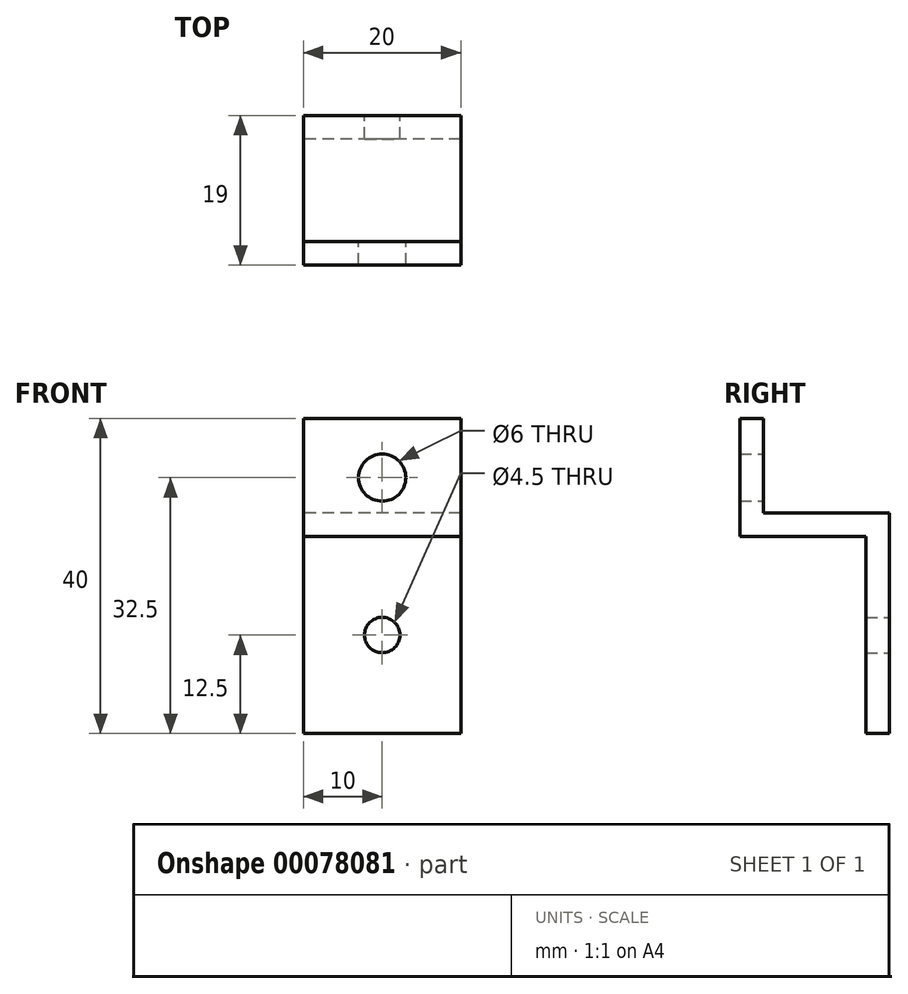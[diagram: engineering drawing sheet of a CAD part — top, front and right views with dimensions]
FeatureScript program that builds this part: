
annotation { "Feature Type Name" : "Feature", "Feature Type Description" : "" }
export const myFeature = defineFeature(function(context is Context, id is Id, definition is map)
    precondition{}
    {
        {
            var Q0;
            Q0=qCreatedBy(makeId("Right.planeOp"),FACE);
            var sketch = newSketch(context, id + "F0", { "sketchPlane" : qUnion([Q0])});
            skLineSegment(sketch, "E0", {"start": v(0, 0) * mm, "end": v(0, 15) * mm});
            skLineSegment(sketch, "E1", {"start": v(0, 15) * mm, "end": v(3, 15) * mm});
            skLineSegment(sketch, "E2", {"start": v(3, 15) * mm, "end": v(3, 3) * mm});
            skLineSegment(sketch, "E3", {"start": v(3, 3) * mm, "end": v(19, 3) * mm});
            skLineSegment(sketch, "E4", {"start": v(19, 3) * mm, "end": v(19, -25) * mm});
            skLineSegment(sketch, "E5", {"start": v(19, -25) * mm, "end": v(16, -25) * mm});
            skLineSegment(sketch, "E6", {"start": v(16, -25) * mm, "end": v(16, 0) * mm});
            skLineSegment(sketch, "E7", {"start": v(16, 0) * mm, "end": v(0, 0) * mm});
            skSolve(sketch);
        }
        {
            var Q0;
            Q0 = qSketchRegion(id + "F0", true);
            extrude(context, id + "F1", {"entities" : qUnion([Q0]), "depth" : 20 * mm, "offsetDistance" : 25 * mm});
        }
        {
            var Q0;
            Q0=makeQuery(id+"F1.opExtrude","SWEPT_FACE",FACE,{"disambiguationData":[OSD([sQuery(id+"F0.wireOp",EDGE,"E0")])]});
            var sketch = newSketch(context, id + "F2", { "sketchPlane" : qUnion([Q0])});
            skPoint(sketch, "E8", {"position": v(10, 7.5) * mm});
            skSolve(sketch);
        }
        {
            var Q0;
            Q0=makeQuery(id+"F1.opExtrude","SWEPT_FACE",FACE,{"disambiguationData":[OSD([sQuery(id+"F0.wireOp",EDGE,"E6")])]});
            var sketch = newSketch(context, id + "F3", { "sketchPlane" : qUnion([Q0])});
            skPoint(sketch, "E9", {"position": v(10, -12.5) * mm});
            skSolve(sketch);
        }
        {
            var Q0;
            Q0=sQuery(id+"F2.wireOp",VERTEX,"E8");
            var Q1;
            Q1=makeQuery(id+"F1.opExtrude","SWEPT_BODY",BODY,{"disambiguationData":[OSD([sQuery(id+"F0.wireOp",EDGE,"E0"),sQuery(id+"F0.wireOp",EDGE,"E1"),sQuery(id+"F0.wireOp",EDGE,"E2"),sQuery(id+"F0.wireOp",EDGE,"E3"),sQuery(id+"F0.wireOp",EDGE,"E4"),sQuery(id+"F0.wireOp",EDGE,"E5"),sQuery(id+"F0.wireOp",EDGE,"E6"),sQuery(id+"F0.wireOp",EDGE,"E7")])]});
            hole(context, id + "F4", {"style" : HoleStyle.SIMPLE, "endStyle" : HoleEndStyle.THROUGH, "holeDiameter" : 6 * mm, "majorDiameter" : 5 * mm, "tappedDepth" : 12 * mm, "tapClearance" : 3, "locations" : qUnion([Q0]), "scope" : qUnion([Q1])});
        }
        {
            var Q0;
            Q0=sQuery(id+"F3.wireOp",VERTEX,"E9");
            var Q1;
            Q1=makeQuery(id+"F1.opExtrude","SWEPT_BODY",BODY,{"disambiguationData":[OSD([sQuery(id+"F0.wireOp",EDGE,"E0"),sQuery(id+"F0.wireOp",EDGE,"E1"),sQuery(id+"F0.wireOp",EDGE,"E2"),sQuery(id+"F0.wireOp",EDGE,"E3"),sQuery(id+"F0.wireOp",EDGE,"E4"),sQuery(id+"F0.wireOp",EDGE,"E5"),sQuery(id+"F0.wireOp",EDGE,"E6"),sQuery(id+"F0.wireOp",EDGE,"E7")])]});
            hole(context, id + "F5", {"style" : HoleStyle.SIMPLE, "endStyle" : HoleEndStyle.THROUGH, "holeDiameter" : 4.5 * mm, "majorDiameter" : 5 * mm, "tappedDepth" : 12 * mm, "tapClearance" : 3, "locations" : qUnion([Q0]), "scope" : qUnion([Q1])});
        }
    });
